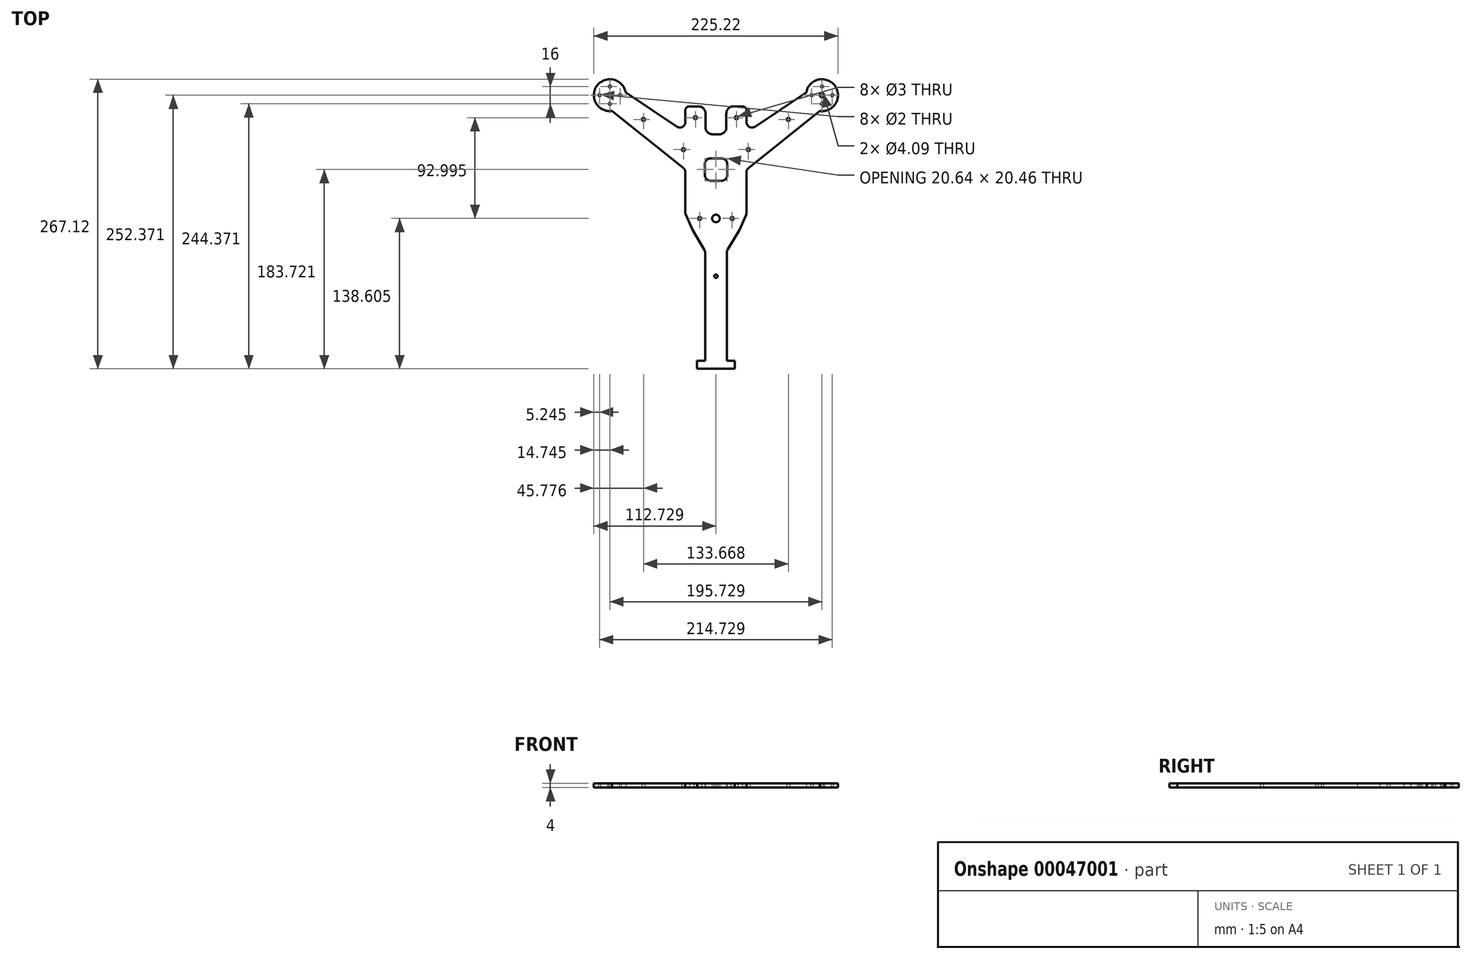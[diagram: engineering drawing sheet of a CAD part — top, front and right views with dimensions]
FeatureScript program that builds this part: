
annotation { "Feature Type Name" : "Feature", "Feature Type Description" : "" }
export const myFeature = defineFeature(function(context is Context, id is Id, definition is map)
    precondition{}
    {
        {
            var Q0;
            Q0=qCreatedBy(makeId("Top.planeOp"),FACE);
            var sketch = newSketch(context, id + "F0", { "sketchPlane" : qUnion([Q0])});
            skLineSegment(sketch, "E0", {"start": v(28.25, 54.56) * mm, "end": v(28.25, 43.92) * mm});
            skLineSegment(sketch, "E1", {"start": v(28.14, -2.4) * mm, "end": v(28.14, -40) * mm});
            skLineSegment(sketch, "E2", {"start": v(27.8, -41.62) * mm, "end": v(21.73, -55.43) * mm});
            skPoint(sketch, "E3.visualSharp", {"position": v(28.25, 58.58) * mm});
            skArc(sketch, "E3.filletArc", {"start": v(28.25, 54.56) * mm, "mid": v(27.15, 57.24) * mm, "end": v(24.5, 58.38) * mm});
            skPoint(sketch, "E4.visualSharp", {"position": v(28.14, -40.84) * mm});
            skArc(sketch, "E4.filletArc", {"start": v(27.8, -41.62) * mm, "mid": v(28.06, -40.83) * mm, "end": v(28.14, -40) * mm});
            skCircle(sketch, "E5", {"center": v(18.93, 48) * mm, "radius": 1.5 * mm});
            skCircle(sketch, "E6", {"center": v(29.96, 18.58) * mm, "radius": 1.5 * mm});
            skCircle(sketch, "E7", {"center": v(15, -45) * mm, "radius": 1.5 * mm});
            skPoint(sketch, "E8.rect.middle", {"position": v(0, 0) * mm});
            skLineSegment(sketch, "E9", {"start": v(24.5, 58.38) * mm, "end": v(15.98, 58.38) * mm});
            skLineSegment(sketch, "E10", {"start": v(0, 32.72) * mm, "end": v(3.32, 32.72) * mm});
            skLineSegment(sketch, "E11", {"start": v(9.65, 39.05) * mm, "end": v(9.65, 52.05) * mm});
            skPoint(sketch, "E12.visualSharp", {"position": v(9.65, 58.38) * mm});
            skArc(sketch, "E12.filletArc", {"start": v(15.98, 58.38) * mm, "mid": v(11.5, 56.53) * mm, "end": v(9.65, 52.05) * mm});
            skPoint(sketch, "E13.visualSharp", {"position": v(9.65, 32.72) * mm});
            skArc(sketch, "E13.filletArc", {"start": v(3.32, 32.72) * mm, "mid": v(7.8, 34.57) * mm, "end": v(9.65, 39.05) * mm});
            skLineSegment(sketch, "E14", {"start": v(30.02, 1.5) * mm, "end": v(110.68, 65.98) * mm});
            skLineSegment(sketch, "E15", {"start": v(111.47, 73.01) * mm, "end": v(105.38, 80.63) * mm});
            skLineSegment(sketch, "E16", {"start": v(98.7, 81.66) * mm, "end": v(36.03, 39.76) * mm});
            skPoint(sketch, "E17.visualSharp", {"position": v(102.5, 84.22) * mm});
            skArc(sketch, "E17.filletArc", {"start": v(105.38, 80.63) * mm, "mid": v(102.24, 82.45) * mm, "end": v(98.7, 81.66) * mm});
            skPoint(sketch, "E18.visualSharp", {"position": v(114.59, 69.1) * mm});
            skArc(sketch, "E18.filletArc", {"start": v(110.68, 65.98) * mm, "mid": v(112.53, 69.33) * mm, "end": v(111.47, 73.01) * mm});
            skPoint(sketch, "E19.visualSharp", {"position": v(28.14, 0) * mm});
            skArc(sketch, "E19.filletArc", {"start": v(30.02, 1.5) * mm, "mid": v(28.64, -0.24) * mm, "end": v(28.14, -2.4) * mm});
            skPoint(sketch, "E20.visualSharp", {"position": v(28.25, 34.56) * mm});
            skArc(sketch, "E20.filletArc", {"start": v(28.25, 43.92) * mm, "mid": v(30.9, 39.5) * mm, "end": v(36.03, 39.76) * mm});
            skLineSegment(sketch, "E21", {"start": v(21.43, -56) * mm, "end": v(10.72, -73.79) * mm});
            skPoint(sketch, "E22.visualSharp", {"position": v(21.6, -55.72) * mm});
            skArc(sketch, "E22.filletArc", {"start": v(21.43, -56) * mm, "mid": v(21.59, -55.71) * mm, "end": v(21.73, -55.43) * mm});
            skPoint(sketch, "E23.visualSharp", {"position": v(10, -74.98) * mm});
            skArc(sketch, "E23.filletArc", {"start": v(10.72, -73.79) * mm, "mid": v(10.18, -75.03) * mm, "end": v(10, -76.37) * mm});
            skCircle(sketch, "E24.MirrorC", {"center": v(-18.93, 48) * mm, "radius": 1.5 * mm});
            skArc(sketch, "E25.MirrorCS", {"start": v(-21.43, -56) * mm, "mid": v(-21.59, -55.71) * mm, "end": v(-21.73, -55.43) * mm});
            skArc(sketch, "E26.MirrorCS", {"start": v(-30.02, 1.5) * mm, "mid": v(-28.64, -0.24) * mm, "end": v(-28.14, -2.4) * mm});
            skArc(sketch, "E27.MirrorCS", {"start": v(-27.8, -41.62) * mm, "mid": v(-28.06, -40.83) * mm, "end": v(-28.14, -40) * mm});
            skArc(sketch, "E28.MirrorCS", {"start": v(-28.25, 54.56) * mm, "mid": v(-27.15, 57.24) * mm, "end": v(-24.5, 58.38) * mm});
            skArc(sketch, "E29.MirrorCS", {"start": v(-10.72, -73.79) * mm, "mid": v(-10.18, -75.03) * mm, "end": v(-10, -76.37) * mm});
            skLineSegment(sketch, "E30.MirrorCS", {"start": v(-28.25, 54.56) * mm, "end": v(-28.25, 43.92) * mm});
            skLineSegment(sketch, "E31.MirrorCS", {"start": v(0, 32.72) * mm, "end": v(-3.32, 32.72) * mm});
            skArc(sketch, "E32.MirrorCS", {"start": v(-105.38, 80.63) * mm, "mid": v(-102.24, 82.45) * mm, "end": v(-98.7, 81.66) * mm});
            skArc(sketch, "E33.MirrorCS", {"start": v(-28.25, 43.92) * mm, "mid": v(-30.9, 39.5) * mm, "end": v(-36.03, 39.76) * mm});
            skLineSegment(sketch, "E34.MirrorCS", {"start": v(-111.47, 73.01) * mm, "end": v(-105.38, 80.63) * mm});
            skCircle(sketch, "E35.MirrorC", {"center": v(-29.96, 18.58) * mm, "radius": 1.5 * mm});
            skArc(sketch, "E36.MirrorCS", {"start": v(-3.32, 32.72) * mm, "mid": v(-7.8, 34.57) * mm, "end": v(-9.65, 39.05) * mm});
            skLineSegment(sketch, "E37.MirrorCS", {"start": v(-24.5, 58.38) * mm, "end": v(-15.98, 58.38) * mm});
            skArc(sketch, "E38.MirrorCS", {"start": v(-15.98, 58.38) * mm, "mid": v(-11.5, 56.53) * mm, "end": v(-9.65, 52.05) * mm});
            skLineSegment(sketch, "E39.MirrorCS", {"start": v(-9.65, 39.05) * mm, "end": v(-9.65, 52.05) * mm});
            skArc(sketch, "E40.MirrorCS", {"start": v(-110.68, 65.98) * mm, "mid": v(-112.53, 69.33) * mm, "end": v(-111.47, 73.01) * mm});
            skCircle(sketch, "E41.MirrorC", {"center": v(-15, -45) * mm, "radius": 1.5 * mm});
            skLineSegment(sketch, "E42.MirrorCS", {"start": v(-27.8, -41.62) * mm, "end": v(-21.73, -55.43) * mm});
            skPoint(sketch, "E43.MirrorP", {"position": v(-9.65, 58.38) * mm});
            skPoint(sketch, "E44.MirrorP", {"position": v(-28.14, 0) * mm});
            skPoint(sketch, "E45.MirrorP", {"position": v(-114.59, 69.1) * mm});
            skLineSegment(sketch, "E46.MirrorCS", {"start": v(-28.14, -2.4) * mm, "end": v(-28.14, -40) * mm});
            skPoint(sketch, "E47.MirrorP", {"position": v(-28.25, 58.58) * mm});
            skLineSegment(sketch, "E48.MirrorCS", {"start": v(-98.7, 81.66) * mm, "end": v(-36.03, 39.76) * mm});
            skPoint(sketch, "E49.MirrorP", {"position": v(-28.25, 34.56) * mm});
            skPoint(sketch, "E50.MirrorP", {"position": v(-9.65, 32.72) * mm});
            skLineSegment(sketch, "E51.MirrorCS", {"start": v(-30.02, 1.5) * mm, "end": v(-110.68, 65.98) * mm});
            skPoint(sketch, "E52.MirrorP", {"position": v(-21.6, -55.72) * mm});
            skPoint(sketch, "E53.MirrorP", {"position": v(-10, -74.98) * mm});
            skPoint(sketch, "E54.MirrorP", {"position": v(-28.14, -40.84) * mm});
            skPoint(sketch, "E55.MirrorP", {"position": v(-102.5, 84.22) * mm});
            skLineSegment(sketch, "E56.MirrorCS", {"start": v(-21.43, -56) * mm, "end": v(-10.72, -73.79) * mm});
            skLineSegment(sketch, "E57", {"start": v(10, -76.37) * mm, "end": v(10, -176.37) * mm});
            skLineSegment(sketch, "E58", {"start": v(10, -176.37) * mm, "end": v(17.56, -176.37) * mm});
            skLineSegment(sketch, "E59", {"start": v(17.56, -176.37) * mm, "end": v(17.56, -183.6) * mm});
            skLineSegment(sketch, "E60", {"start": v(17.56, -183.6) * mm, "end": v(0, -183.6) * mm});
            skLineSegment(sketch, "E61.MirrorCS", {"start": v(-17.56, -176.37) * mm, "end": v(-17.56, -183.6) * mm});
            skLineSegment(sketch, "E62.MirrorCS", {"start": v(-17.56, -183.6) * mm, "end": v(0, -183.6) * mm});
            skLineSegment(sketch, "E63.MirrorCS", {"start": v(-10, -176.37) * mm, "end": v(-17.56, -176.37) * mm});
            skLineSegment(sketch, "E64.MirrorCS", {"start": v(-10, -76.37) * mm, "end": v(-10, -176.37) * mm});
            skCircle(sketch, "E65", {"center": v(97.86, 68.77) * mm, "radius": 2.04 * mm});
            skCircle(sketch, "E66", {"center": v(97.86, 76.77) * mm, "radius": 1 * mm});
            skCircle(sketch, "E67", {"center": v(107.36, 68.77) * mm, "radius": 1 * mm});
            skCircle(sketch, "E68.MirrorC", {"center": v(97.86, 60.77) * mm, "radius": 1 * mm});
            skCircle(sketch, "E69.MirrorC", {"center": v(88.36, 68.77) * mm, "radius": 1 * mm});
            skCircle(sketch, "E70.MirrorC", {"center": v(-97.86, 60.77) * mm, "radius": 1 * mm});
            skCircle(sketch, "E71.MirrorC", {"center": v(-107.36, 68.77) * mm, "radius": 1 * mm});
            skCircle(sketch, "E72.MirrorC", {"center": v(-88.36, 68.77) * mm, "radius": 1 * mm});
            skCircle(sketch, "E73.MirrorC", {"center": v(-97.86, 68.77) * mm, "radius": 2.04 * mm});
            skCircle(sketch, "E74.MirrorC", {"center": v(-97.86, 76.77) * mm, "radius": 1 * mm});
            skCircle(sketch, "E75", {"center": v(97.86, 68.77) * mm, "radius": 14.75 * mm});
            skCircle(sketch, "E76.MirrorC", {"center": v(-97.86, 68.77) * mm, "radius": 14.75 * mm});
            skLineSegment(sketch, "E77.bottom", {"start": v(-5.2, 10.35) * mm, "end": v(5.44, 10.35) * mm});
            skLineSegment(sketch, "E77.top", {"start": v(-5.2, -10.1) * mm, "end": v(5.44, -10.1) * mm});
            skLineSegment(sketch, "E77.left", {"start": v(-10.2, 5.35) * mm, "end": v(-10.2, -5.1) * mm});
            skLineSegment(sketch, "E77.right", {"start": v(10.44, 5.35) * mm, "end": v(10.44, -5.1) * mm});
            skPoint(sketch, "E78.visualSharp", {"position": v(-10.2, 10.35) * mm});
            skArc(sketch, "E78.filletArc", {"start": v(-5.2, 10.35) * mm, "mid": v(-8.74, 8.88) * mm, "end": v(-10.2, 5.35) * mm});
            skPoint(sketch, "E79.visualSharp", {"position": v(10.44, 10.35) * mm});
            skArc(sketch, "E79.filletArc", {"start": v(10.44, 5.35) * mm, "mid": v(8.97, 8.88) * mm, "end": v(5.44, 10.35) * mm});
            skPoint(sketch, "E80.visualSharp", {"position": v(10.44, -10.1) * mm});
            skArc(sketch, "E80.filletArc", {"start": v(5.44, -10.1) * mm, "mid": v(8.97, -8.64) * mm, "end": v(10.44, -5.1) * mm});
            skPoint(sketch, "E81.visualSharp", {"position": v(-10.2, -10.1) * mm});
            skArc(sketch, "E81.filletArc", {"start": v(-10.2, -5.1) * mm, "mid": v(-8.74, -8.64) * mm, "end": v(-5.2, -10.1) * mm});
            skCircle(sketch, "E82", {"center": v(66.83, 46.38) * mm, "radius": 1.5 * mm});
            skCircle(sketch, "E83", {"center": v(0.1, -98.25) * mm, "radius": 1.5 * mm});
            skCircle(sketch, "E84.MirrorC", {"center": v(-0.1, -98.25) * mm, "radius": 1.5 * mm});
            skCircle(sketch, "E85.MirrorC", {"center": v(-66.83, 46.38) * mm, "radius": 1.5 * mm});
            skCircle(sketch, "E86", {"center": v(0, -44.97) * mm, "radius": 3.5 * mm});
            skSolve(sketch);
        }
        {
            var Q0;
            Q0 = qSketchRegion(id + "F0", true);
            extrude(context, id + "F1", {"entities" : qUnion([Q0]), "depth" : 4 * mm});
        }
    });
